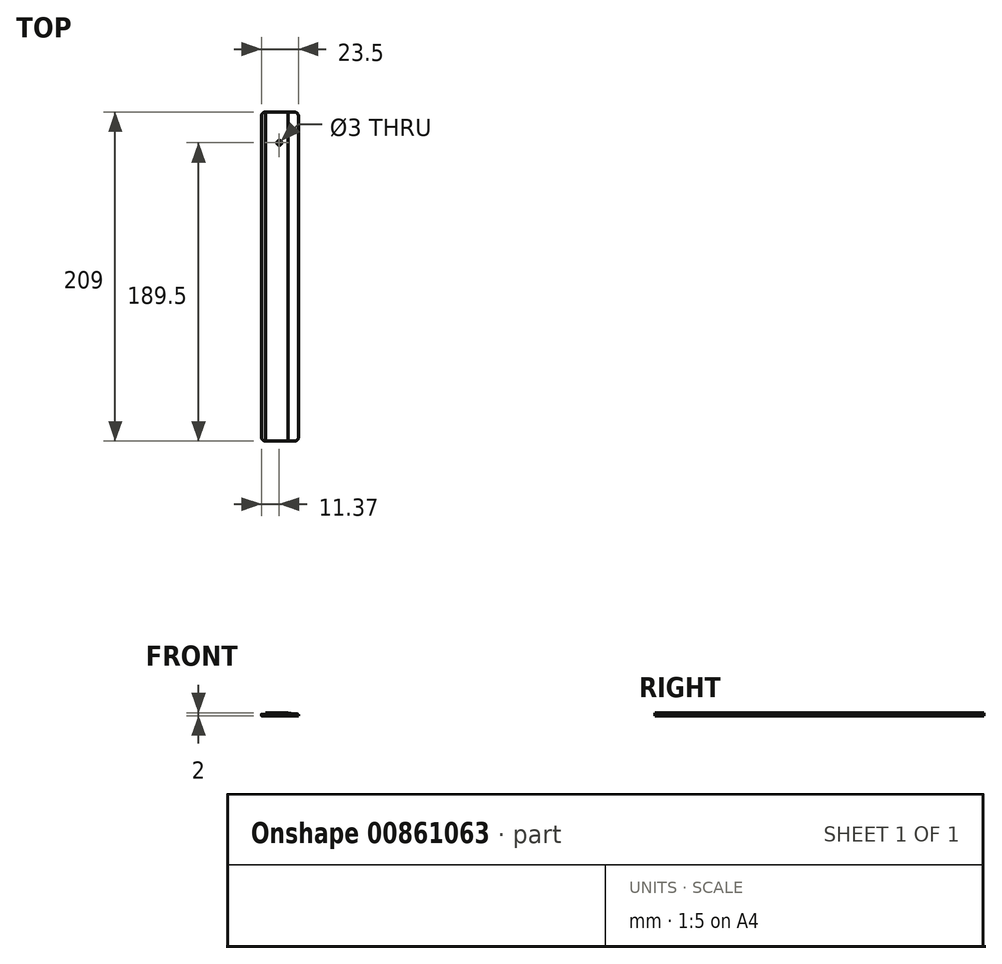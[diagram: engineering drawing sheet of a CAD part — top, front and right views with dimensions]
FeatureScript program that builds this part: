
annotation { "Feature Type Name" : "Feature", "Feature Type Description" : "" }
export const myFeature = defineFeature(function(context is Context, id is Id, definition is map)
    precondition{}
    {
        {
            var Q0;
            Q0=qCreatedBy(makeId("Front.planeOp"),FACE);
            var sketch = newSketch(context, id + "F0", { "sketchPlane" : qUnion([Q0])});
            skLineSegment(sketch, "E0", {"start": v(-11.37, -1.27) * mm, "end": v(-11.37, -0.27) * mm});
            skLineSegment(sketch, "E1", {"start": v(-8.87, 0.73) * mm, "end": v(5.63, 0.73) * mm});
            skLineSegment(sketch, "E2", {"start": v(5.63, 0.73) * mm, "end": v(12.13, -0.27) * mm});
            skLineSegment(sketch, "E3", {"start": v(12.13, -0.27) * mm, "end": v(12.13, -1.27) * mm});
            skLineSegment(sketch, "E4", {"start": v(12.13, -1.27) * mm, "end": v(-11.37, -1.27) * mm});
            skLineSegment(sketch, "E5", {"start": v(-11.37, -0.27) * mm, "end": v(-8.87, -0.27) * mm});
            skLineSegment(sketch, "E6", {"start": v(-8.87, -0.27) * mm, "end": v(-8.87, 0.73) * mm});
            skPoint(sketch, "E7.orphan", {"position": v(-11.37, 0.73) * mm});
            skSolve(sketch);
        }
        {
            var Q0;
            Q0 = qSketchRegion(id + "F0", true);
            extrude(context, id + "F1", {"entities" : qUnion([Q0]), "depth" : 209 * mm, "offsetDistance" : 25 * mm, "symmetric" : true});
        }
        {
            var Q0;
            Q0=makeQuery(id+"F1.opExtrude","SWEPT_FACE",FACE,{"disambiguationData":[OSD([sQuery(id+"F0.wireOp",EDGE,"E1")])]});
            var sketch = newSketch(context, id + "F2", { "sketchPlane" : qUnion([Q0])});
            skCircle(sketch, "E8", {"center": v(0, 85) * mm, "radius": 1.5 * mm});
            skSolve(sketch);
        }
        {
            var Q0;
            Q0=makeQuery(id+"F2.imprint","IMPRINT",FACE,{"disambiguationData":[TD([[makeQuery(id+"F2.imprint","IMPRINT",EDGE,{"derivedFrom":sQuery(id+"F2.wireOp",EDGE,"E8")}),1.0]])]});
            extrude(context, id + "F3", {"entities" : qUnion([Q0]), "operationType" : NewBodyOperationType.REMOVE, "oppositeDirection" : true, "depth" : 2 * mm, "offsetDistance" : 25 * mm});
        }
        {
            var Q0;
            Q0=makeQuery(id+"F1.opExtrude","CAP_EDGE",EDGE,{"disambiguationData":[OSD([sQuery(id+"F0.wireOp",EDGE,"E3")])],"isStart":true});
            var Q1;
            Q1=makeQuery(id+"F1.opExtrude","CAP_EDGE",EDGE,{"disambiguationData":[OSD([sQuery(id+"F0.wireOp",EDGE,"E0")])],"isStart":true});
            var Q2;
            Q2=makeQuery(id+"F1.opExtrude","CAP_EDGE",EDGE,{"disambiguationData":[OSD([sQuery(id+"F0.wireOp",EDGE,"E3")])],"isStart":false});
            var Q3;
            Q3=makeQuery(id+"F1.opExtrude","CAP_EDGE",EDGE,{"disambiguationData":[OSD([sQuery(id+"F0.wireOp",EDGE,"E0")])],"isStart":false});
            fillet(context, id + "F4", {"entities" : qUnion([Q0, Q1, Q2, Q3]), "radius" : 2.5 * mm, "tangentPropagation" : true, "allowEdgeOverflow" : false});
        }
    });
